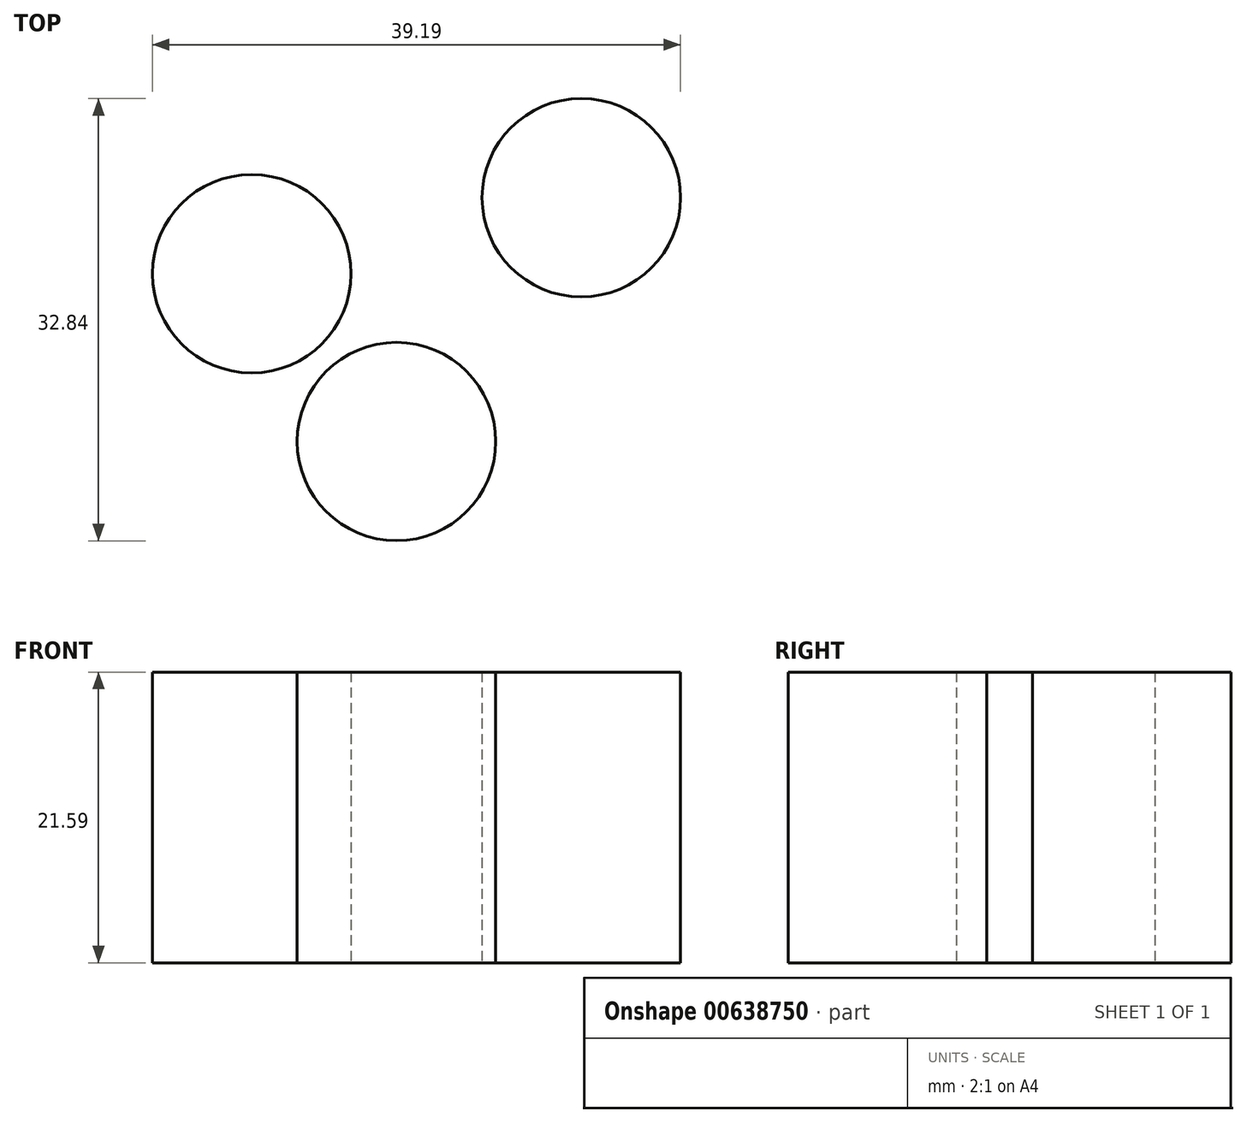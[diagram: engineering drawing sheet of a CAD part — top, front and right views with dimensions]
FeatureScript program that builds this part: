
annotation { "Feature Type Name" : "Feature", "Feature Type Description" : "" }
export const myFeature = defineFeature(function(context is Context, id is Id, definition is map)
    precondition{}
    {
        {
            var Q0;
            Q0=qCreatedBy(makeId("Top.planeOp"),FACE);
            var sketch = newSketch(context, id + "F0", { "sketchPlane" : qUnion([Q0])});
            skCircle(sketch, "E0", {"center": v(0, 0) * mm, "radius": 7.37 * mm});
            skCircle(sketch, "E1", {"center": v(-10.74, 12.46) * mm, "radius": 7.37 * mm});
            skCircle(sketch, "E2", {"center": v(13.72, 18.1) * mm, "radius": 7.37 * mm});
            skSolve(sketch);
        }
        {
            var Q0;
            Q0=makeQuery(id+"F0.imprint","IMPRINT",FACE,{"disambiguationData":[TD([[makeQuery(id+"F0.imprint","IMPRINT",EDGE,{"derivedFrom":sQuery(id+"F0.wireOp",EDGE,"E1")}),1.0]])]});
            var Q1;
            Q1=makeQuery(id+"F0.imprint","IMPRINT",FACE,{"disambiguationData":[TD([[makeQuery(id+"F0.imprint","IMPRINT",EDGE,{"derivedFrom":sQuery(id+"F0.wireOp",EDGE,"E0")}),1.0]])]});
            var Q2;
            Q2=makeQuery(id+"F0.imprint","IMPRINT",FACE,{"disambiguationData":[TD([[makeQuery(id+"F0.imprint","IMPRINT",EDGE,{"derivedFrom":sQuery(id+"F0.wireOp",EDGE,"E2")}),1.0]])]});
            extrude(context, id + "F1", {"entities" : qUnion([Q0, Q1, Q2]), "depth" : 21.59 * mm, "offsetDistance" : 25.4 * mm});
        }
    });
